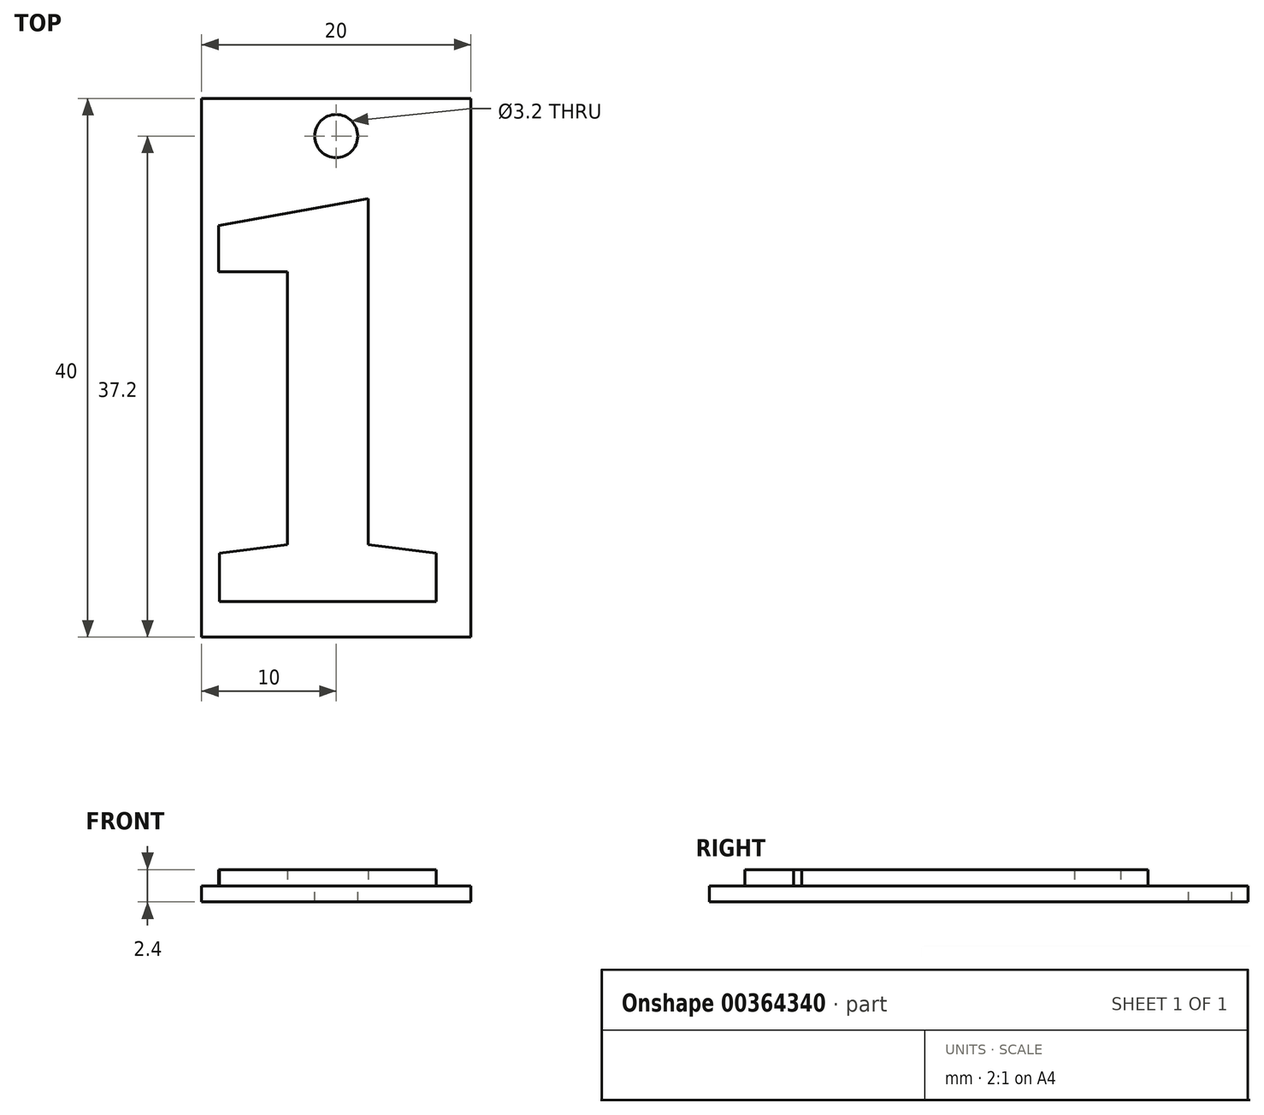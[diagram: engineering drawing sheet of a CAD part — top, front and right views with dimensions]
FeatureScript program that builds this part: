
annotation { "Feature Type Name" : "Feature", "Feature Type Description" : "" }
export const myFeature = defineFeature(function(context is Context, id is Id, definition is map)
    precondition{}
    {
        {
            var Q0;
            Q0=qCreatedBy(makeId("Top.planeOp"),FACE);
            var sketch = newSketch(context, id + "F0", { "sketchPlane" : qUnion([Q0])});
            skLineSegment(sketch, "E0.bottom", {"start": v(10, -20) * mm, "end": v(-10, -20) * mm});
            skLineSegment(sketch, "E0.top", {"start": v(10, 20) * mm, "end": v(-10, 20) * mm});
            skLineSegment(sketch, "E0.left", {"start": v(10, -20) * mm, "end": v(10, 20) * mm});
            skLineSegment(sketch, "E0.right", {"start": v(-10, -20) * mm, "end": v(-10, 20) * mm});
            skPoint(sketch, "E0.middle", {"position": v(0, 0) * mm});
            skCircle(sketch, "E1", {"center": v(0, 17.2) * mm, "radius": 1.6 * mm});
            skLineSegment(sketch, "E2", {"start": v(0, -20) * mm, "end": v(0, 15.6) * mm, "construction": true});
            skText(sketch, "E3", { "text": "1", "fontName": "RobotoSlab-Bold.ttf"});
            skLineSegment(sketch, "E4", {"start": v(-10, -2.2) * mm, "end": v(10, -2.2) * mm, "construction": true});
            skPoint(sketch, "E4.startSnap0", {"position": v(0, -2.2) * mm});
            skLineSegment(sketch, "E5", {"start": v(10, -2.2) * mm, "end": v(-10, -2.2) * mm, "construction": true});
            const initialGuessF0  = {"E3": [-0.01, -0.01735, 1, 0, 0.0303]};
            skSetInitialGuess(sketch, initialGuessF0);
            skSolve(sketch);
        }
        {
            var Q0;
            Q0 = qSketchRegion(id + "F0", true);
            var Q1;
            Q1=makeQuery(id+"F0.imprint","IMPRINT",FACE,{"disambiguationData":[TD([[makeQuery(id+"F0.imprint","IMPRINT",EDGE,{"derivedFrom":sQuery(id+"F0.wireOp",EDGE,"E3.sketch_text.stroke-0")}),-1.0]])]});
            extrude(context, id + "F1", {"entities" : qUnion([Q0, Q1]), "oppositeDirection" : true, "depth" : 1.2 * mm});
        }
        {
            var Q0;
            Q0=makeQuery(id+"F0.imprint","IMPRINT",FACE,{"disambiguationData":[TD([[makeQuery(id+"F0.imprint","IMPRINT",EDGE,{"derivedFrom":sQuery(id+"F0.wireOp",EDGE,"E3.sketch_text.stroke-0")}),-1.0]])]});
            extrude(context, id + "F2", {"entities" : qUnion([Q0]), "operationType" : NewBodyOperationType.ADD, "depth" : 1.2 * mm});
        }
    });
